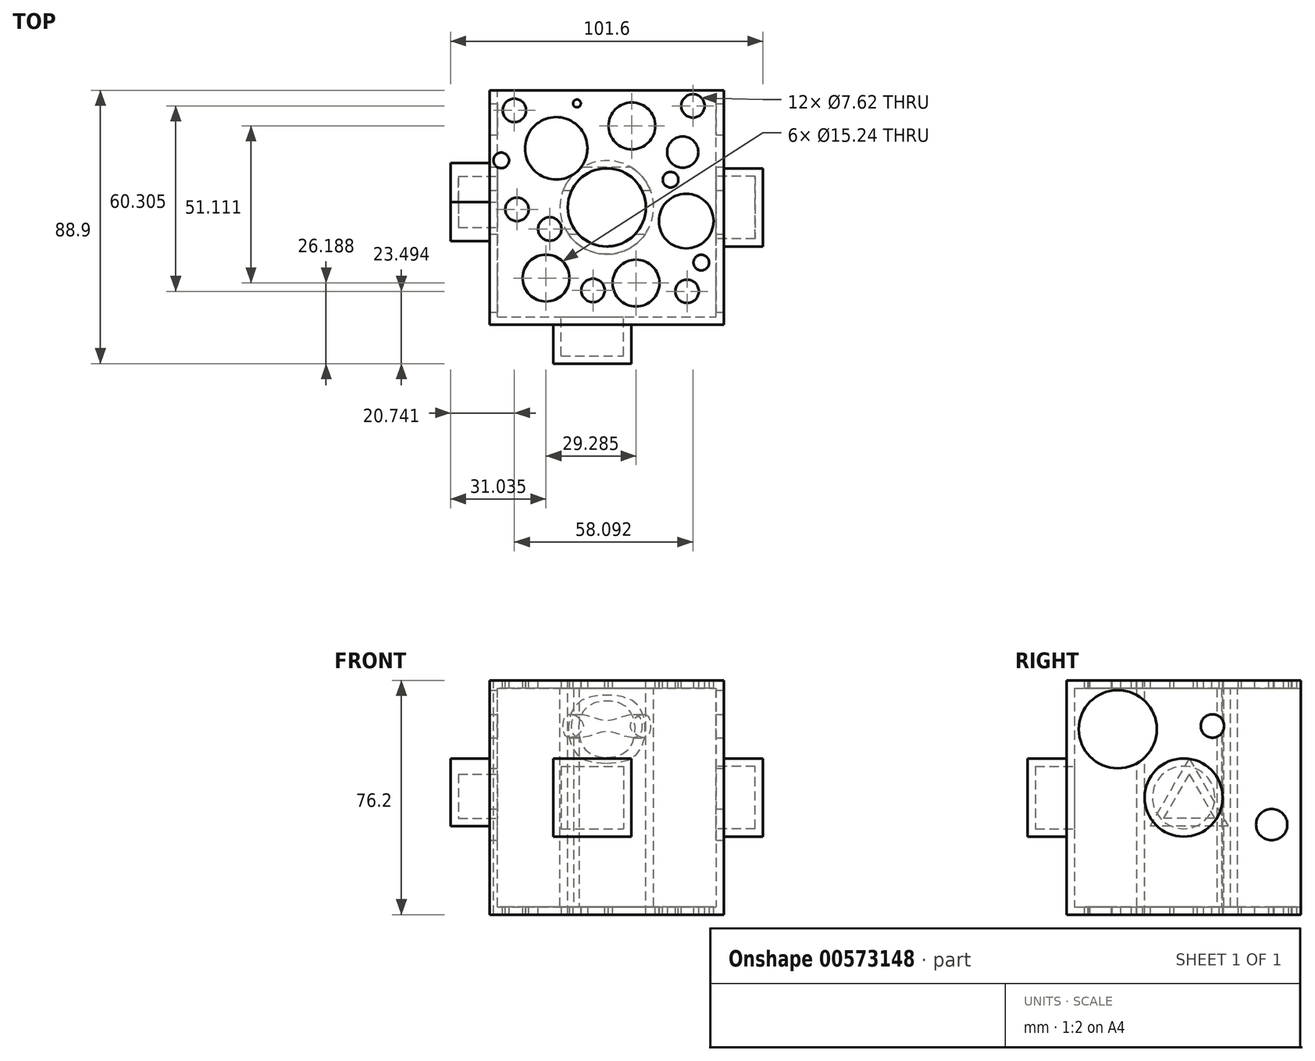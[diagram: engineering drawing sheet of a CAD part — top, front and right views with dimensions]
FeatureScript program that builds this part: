
annotation { "Feature Type Name" : "Feature", "Feature Type Description" : "" }
export const myFeature = defineFeature(function(context is Context, id is Id, definition is map)
    precondition{}
    {
        {
            var Q0;
            Q0=qCreatedBy(makeId("Front.planeOp"),FACE);
            var sketch = newSketch(context, id + "F0", { "sketchPlane" : qUnion([Q0])});
            skLineSegment(sketch, "E0.bottom", {"start": v(-76.2, 76.2) * mm, "end": v(0, 76.2) * mm});
            skLineSegment(sketch, "E0.top", {"start": v(-76.2, 0) * mm, "end": v(0, 0) * mm});
            skLineSegment(sketch, "E0.left", {"start": v(-76.2, 76.2) * mm, "end": v(-76.2, 0) * mm});
            skLineSegment(sketch, "E0.right", {"start": v(0, 76.2) * mm, "end": v(0, 0) * mm});
            skSolve(sketch);
        }
        {
            var Q0;
            Q0=makeQuery(id+"F0.imprint","IMPRINT",FACE,{"disambiguationData":[TD([[makeQuery(id+"F0.imprint","IMPRINT",EDGE,{"derivedFrom":sQuery(id+"F0.wireOp",EDGE,"E0.bottom")}),-1.0]])]});
            extrude(context, id + "F1", {"entities" : qUnion([Q0]), "depth" : 76.2 * mm, "offsetDistance" : 25.4 * mm});
        }
        {
            var Q0;
            Q0=makeQuery(id+"F1.opExtrude","CAP_FACE",FACE,{"disambiguationData":[OSD([sQuery(id+"F0.wireOp",EDGE,"E0.bottom"),sQuery(id+"F0.wireOp",EDGE,"E0.top"),sQuery(id+"F0.wireOp",EDGE,"E0.left"),sQuery(id+"F0.wireOp",EDGE,"E0.right")])],"isStart":false});
            var sketch = newSketch(context, id + "F2", { "sketchPlane" : qUnion([Q0])});
            skLineSegment(sketch, "E1.bottom", {"start": v(-55.52, 50.8) * mm, "end": v(-30.12, 50.8) * mm});
            skLineSegment(sketch, "E1.top", {"start": v(-55.52, 25.4) * mm, "end": v(-30.12, 25.4) * mm});
            skLineSegment(sketch, "E1.left", {"start": v(-55.52, 50.8) * mm, "end": v(-55.52, 25.4) * mm});
            skLineSegment(sketch, "E1.right", {"start": v(-30.12, 50.8) * mm, "end": v(-30.12, 25.4) * mm});
            skSolve(sketch);
        }
        {
            var Q0;
            Q0=makeQuery(id+"F2.imprint","IMPRINT",FACE,{"disambiguationData":[TD([[makeQuery(id+"F2.imprint","IMPRINT",EDGE,{"derivedFrom":sQuery(id+"F2.wireOp",EDGE,"E1.bottom")}),-1.0]])]});
            extrude(context, id + "F3", {"entities" : qUnion([Q0]), "operationType" : NewBodyOperationType.ADD, "depth" : 12.7 * mm, "offsetDistance" : 25.4 * mm});
        }
        {
            var Q0;
            Q0=makeQuery(id+"F1.opExtrude","SWEPT_FACE",FACE,{"disambiguationData":[OSD([sQuery(id+"F0.wireOp",EDGE,"E0.right")])]});
            var sketch = newSketch(context, id + "F4", { "sketchPlane" : qUnion([Q0])});
            skCircle(sketch, "E2", {"center": v(-38.1, 38.1) * mm, "radius": 12.7 * mm});
            skSolve(sketch);
        }
        {
            var Q0;
            Q0=makeQuery(id+"F4.imprint","IMPRINT",FACE,{"disambiguationData":[TD([[makeQuery(id+"F4.imprint","IMPRINT",EDGE,{"derivedFrom":sQuery(id+"F4.wireOp",EDGE,"E2")}),1.0]])]});
            extrude(context, id + "F5", {"entities" : qUnion([Q0]), "operationType" : NewBodyOperationType.ADD, "depth" : 12.7 * mm, "offsetDistance" : 25.4 * mm});
        }
        {
            var Q0;
            Q0=makeQuery(id+"F1.opExtrude","SWEPT_FACE",FACE,{"disambiguationData":[OSD([sQuery(id+"F0.wireOp",EDGE,"E0.bottom")])]});
            var sketch = newSketch(context, id + "F6", { "sketchPlane" : qUnion([Q0])});
            skPoint(sketch, "E3", {"position": v(-38.1, -38.1) * mm});
            skSolve(sketch);
        }
        {
            var Q0;
            Q0=sQuery(id+"F6.wireOp",VERTEX,"E3");
            var Q1;
            Q1=makeQuery(id+"F1.opExtrude","SWEPT_BODY",BODY,{"disambiguationData":[OSD([sQuery(id+"F0.wireOp",EDGE,"E0.bottom"),sQuery(id+"F0.wireOp",EDGE,"E0.top"),sQuery(id+"F0.wireOp",EDGE,"E0.left"),sQuery(id+"F0.wireOp",EDGE,"E0.right")])]});
            hole(context, id + "F7", {"style" : HoleStyle.SIMPLE, "endStyle" : HoleEndStyle.THROUGH, "holeDiameter" : 25.4 * mm, "isTappedThrough" : true, "tappedDepth" : 12.7 * mm, "tapClearance" : 3, "locations" : qUnion([Q0]), "scope" : qUnion([Q1])});
        }
        {
            var Q0;
            Q0=makeQuery(id+"F1.opExtrude","SWEPT_FACE",FACE,{"disambiguationData":[OSD([sQuery(id+"F0.wireOp",EDGE,"E0.left")])]});
            var sketch = newSketch(context, id + "F8", { "sketchPlane" : qUnion([Q0])});
            skLineSegment(sketch, "E4", {"start": v(36.34, 50.8) * mm, "end": v(23.64, 28.8) * mm});
            skLineSegment(sketch, "E5", {"start": v(23.64, 28.8) * mm, "end": v(49.04, 28.8) * mm});
            skLineSegment(sketch, "E6", {"start": v(36.34, 50.8) * mm, "end": v(49.04, 28.8) * mm});
            skSolve(sketch);
        }
        {
            var Q0;
            Q0=makeQuery(id+"F8.imprint","IMPRINT",FACE,{"disambiguationData":[TD([[makeQuery(id+"F8.imprint","IMPRINT",EDGE,{"derivedFrom":sQuery(id+"F8.wireOp",EDGE,"E4")}),1.0]])]});
            extrude(context, id + "F9", {"entities" : qUnion([Q0]), "operationType" : NewBodyOperationType.ADD, "depth" : 12.7 * mm, "offsetDistance" : 25.4 * mm});
        }
        {
            var Q0;
            Q0=makeQuery(id+"F1.opExtrude","CAP_FACE",FACE,{"disambiguationData":[OSD([sQuery(id+"F0.wireOp",EDGE,"E0.bottom"),sQuery(id+"F0.wireOp",EDGE,"E0.top"),sQuery(id+"F0.wireOp",EDGE,"E0.left"),sQuery(id+"F0.wireOp",EDGE,"E0.right")])],"isStart":true});
            var sketch = newSketch(context, id + "F10", { "sketchPlane" : qUnion([Q0])});
            skSolve(sketch);
        }
        {
            var Q0;
            Q0=makeQuery(id+"F1.opExtrude","CAP_FACE",FACE,{"disambiguationData":[OSD([sQuery(id+"F0.wireOp",EDGE,"E0.bottom"),sQuery(id+"F0.wireOp",EDGE,"E0.top"),sQuery(id+"F0.wireOp",EDGE,"E0.left"),sQuery(id+"F0.wireOp",EDGE,"E0.right")])],"isStart":true});
            shell(context, id + "F11", {"entities" : qUnion([Q0]), "thickness" : 2.54 * mm});
        }
        {
            var Q0;
            Q0=makeQuery(id+"F1.opExtrude","SWEPT_FACE",FACE,{"disambiguationData":[OSD([sQuery(id+"F0.wireOp",EDGE,"E0.top")])]});
            var sketch = newSketch(context, id + "F12", { "sketchPlane" : qUnion([Q0])});
            skPoint(sketch, "E7", {"position": v(-7.34, 56.06) * mm});
            skSolve(sketch);
        }
        {
            var Q0;
            Q0=sQuery(id+"F12.wireOp",VERTEX,"E7");
            var Q1;
            Q1=makeQuery(id+"F1.opExtrude","SWEPT_BODY",BODY,{"disambiguationData":[OSD([sQuery(id+"F0.wireOp",EDGE,"E0.bottom"),sQuery(id+"F0.wireOp",EDGE,"E0.top"),sQuery(id+"F0.wireOp",EDGE,"E0.left"),sQuery(id+"F0.wireOp",EDGE,"E0.right")])]});
            hole(context, id + "F13", {"style" : HoleStyle.SIMPLE, "endStyle" : HoleEndStyle.THROUGH, "holeDiameter" : 5.08 * mm, "majorDiameter" : 6.35 * mm, "isTappedThrough" : true, "tappedDepth" : 12.7 * mm, "tapClearance" : 3, "locations" : qUnion([Q0]), "scope" : qUnion([Q1])});
        }
        {
            var Q0;
            Q0=makeQuery(id+"F1.opExtrude","SWEPT_FACE",FACE,{"disambiguationData":[OSD([sQuery(id+"F0.wireOp",EDGE,"E0.top")])]});
            var sketch = newSketch(context, id + "F14", { "sketchPlane" : qUnion([Q0])});
            skPoint(sketch, "E8", {"position": v(-13.4, 20.13) * mm});
            skSolve(sketch);
        }
        {
            var Q0;
            Q0=sQuery(id+"F14.wireOp",VERTEX,"E8");
            var Q1;
            Q1=makeQuery(id+"F1.opExtrude","SWEPT_BODY",BODY,{"disambiguationData":[OSD([sQuery(id+"F0.wireOp",EDGE,"E0.bottom"),sQuery(id+"F0.wireOp",EDGE,"E0.top"),sQuery(id+"F0.wireOp",EDGE,"E0.left"),sQuery(id+"F0.wireOp",EDGE,"E0.right")])]});
            hole(context, id + "F15", {"style" : HoleStyle.SIMPLE, "endStyle" : HoleEndStyle.THROUGH, "holeDiameter" : 10.16 * mm, "majorDiameter" : 6.35 * mm, "isTappedThrough" : true, "tappedDepth" : 12.7 * mm, "tapClearance" : 3, "locations" : qUnion([Q0]), "scope" : qUnion([Q1])});
        }
        {
            var Q0;
            Q0=makeQuery(id+"F1.opExtrude","SWEPT_FACE",FACE,{"disambiguationData":[OSD([sQuery(id+"F0.wireOp",EDGE,"E0.top")])]});
            var sketch = newSketch(context, id + "F16", { "sketchPlane" : qUnion([Q0])});
            skPoint(sketch, "E9", {"position": v(-54.55, 18.9) * mm});
            skSolve(sketch);
        }
        {
            var Q0;
            Q0=sQuery(id+"F16.wireOp",VERTEX,"E9");
            var Q1;
            Q1=makeQuery(id+"F1.opExtrude","SWEPT_BODY",BODY,{"disambiguationData":[OSD([sQuery(id+"F0.wireOp",EDGE,"E0.bottom"),sQuery(id+"F0.wireOp",EDGE,"E0.top"),sQuery(id+"F0.wireOp",EDGE,"E0.left"),sQuery(id+"F0.wireOp",EDGE,"E0.right")])]});
            hole(context, id + "F17", {"style" : HoleStyle.SIMPLE, "endStyle" : HoleEndStyle.THROUGH, "holeDiameter" : 20.32 * mm, "majorDiameter" : 6.35 * mm, "isTappedThrough" : true, "tappedDepth" : 12.7 * mm, "tapClearance" : 3, "locations" : qUnion([Q0]), "scope" : qUnion([Q1])});
        }
        {
            var Q0;
            Q0=makeQuery(id+"F1.opExtrude","SWEPT_FACE",FACE,{"disambiguationData":[OSD([sQuery(id+"F0.wireOp",EDGE,"E0.top")])]});
            var sketch = newSketch(context, id + "F18", { "sketchPlane" : qUnion([Q0])});
            skPoint(sketch, "E10", {"position": v(-57.87, 61.09) * mm});
            skSolve(sketch);
        }
        {
            var Q0;
            Q0=sQuery(id+"F18.wireOp",VERTEX,"E10");
            var Q1;
            Q1=makeQuery(id+"F1.opExtrude","SWEPT_BODY",BODY,{"disambiguationData":[OSD([sQuery(id+"F0.wireOp",EDGE,"E0.bottom"),sQuery(id+"F0.wireOp",EDGE,"E0.top"),sQuery(id+"F0.wireOp",EDGE,"E0.left"),sQuery(id+"F0.wireOp",EDGE,"E0.right")])]});
            hole(context, id + "F19", {"style" : HoleStyle.SIMPLE, "endStyle" : HoleEndStyle.THROUGH, "holeDiameter" : 15.24 * mm, "majorDiameter" : 6.35 * mm, "isTappedThrough" : true, "tappedDepth" : 12.7 * mm, "tapClearance" : 3, "locations" : qUnion([Q0]), "scope" : qUnion([Q1])});
        }
        {
            var Q0;
            Q0=makeQuery(id+"F1.opExtrude","SWEPT_FACE",FACE,{"disambiguationData":[OSD([sQuery(id+"F0.wireOp",EDGE,"E0.bottom")])]});
            var sketch = newSketch(context, id + "F20", { "sketchPlane" : qUnion([Q0])});
            skPoint(sketch, "E11", {"position": v(-67.32, -38.75) * mm});
            skSolve(sketch);
        }
        {
            var Q0;
            Q0=sQuery(id+"F20.wireOp",VERTEX,"E11");
            var Q1;
            Q1=makeQuery(id+"F1.opExtrude","SWEPT_BODY",BODY,{"disambiguationData":[OSD([sQuery(id+"F0.wireOp",EDGE,"E0.bottom"),sQuery(id+"F0.wireOp",EDGE,"E0.top"),sQuery(id+"F0.wireOp",EDGE,"E0.left"),sQuery(id+"F0.wireOp",EDGE,"E0.right")])]});
            hole(context, id + "F21", {"style" : HoleStyle.SIMPLE, "endStyle" : HoleEndStyle.THROUGH, "holeDiameter" : 7.62 * mm, "majorDiameter" : 6.35 * mm, "isTappedThrough" : true, "tappedDepth" : 12.7 * mm, "tapClearance" : 3, "locations" : qUnion([Q0]), "scope" : qUnion([Q1])});
        }
        {
            var Q0;
            Q0=makeQuery(id+"F1.opExtrude","SWEPT_FACE",FACE,{"disambiguationData":[OSD([sQuery(id+"F0.wireOp",EDGE,"E0.bottom")])]});
            var sketch = newSketch(context, id + "F22", { "sketchPlane" : qUnion([Q0])});
            skPoint(sketch, "E12", {"position": v(-28.58, -62.71) * mm});
            skSolve(sketch);
        }
        {
            var Q0;
            Q0=sQuery(id+"F22.wireOp",VERTEX,"E12");
            var Q1;
            Q1=makeQuery(id+"F1.opExtrude","SWEPT_BODY",BODY,{"disambiguationData":[OSD([sQuery(id+"F0.wireOp",EDGE,"E0.bottom"),sQuery(id+"F0.wireOp",EDGE,"E0.top"),sQuery(id+"F0.wireOp",EDGE,"E0.left"),sQuery(id+"F0.wireOp",EDGE,"E0.right")])]});
            hole(context, id + "F23", {"style" : HoleStyle.SIMPLE, "endStyle" : HoleEndStyle.THROUGH, "holeDiameter" : 15.24 * mm, "majorDiameter" : 6.35 * mm, "isTappedThrough" : true, "tappedDepth" : 12.7 * mm, "tapClearance" : 3, "locations" : qUnion([Q0]), "scope" : qUnion([Q1])});
        }
        {
            var Q0;
            Q0=makeQuery(id+"F1.opExtrude","SWEPT_FACE",FACE,{"disambiguationData":[OSD([sQuery(id+"F0.wireOp",EDGE,"E0.bottom")])]});
            var sketch = newSketch(context, id + "F24", { "sketchPlane" : qUnion([Q0])});
            skPoint(sketch, "E13", {"position": v(-29.94, -11.6) * mm});
            skSolve(sketch);
        }
        {
            var Q0;
            Q0=sQuery(id+"F24.wireOp",VERTEX,"E13");
            var Q1;
            Q1=makeQuery(id+"F1.opExtrude","SWEPT_BODY",BODY,{"disambiguationData":[OSD([sQuery(id+"F0.wireOp",EDGE,"E0.bottom"),sQuery(id+"F0.wireOp",EDGE,"E0.top"),sQuery(id+"F0.wireOp",EDGE,"E0.left"),sQuery(id+"F0.wireOp",EDGE,"E0.right")])]});
            hole(context, id + "F25", {"style" : HoleStyle.SIMPLE, "endStyle" : HoleEndStyle.THROUGH, "holeDiameter" : 15.24 * mm, "majorDiameter" : 6.35 * mm, "isTappedThrough" : true, "tappedDepth" : 12.7 * mm, "tapClearance" : 3, "locations" : qUnion([Q0]), "scope" : qUnion([Q1])});
        }
        {
            var Q0;
            Q0=makeQuery(id+"F1.opExtrude","SWEPT_FACE",FACE,{"disambiguationData":[OSD([sQuery(id+"F0.wireOp",EDGE,"E0.bottom")])]});
            var sketch = newSketch(context, id + "F26", { "sketchPlane" : qUnion([Q0])});
            skPoint(sketch, "E14", {"position": v(-12.26, -42.55) * mm});
            skSolve(sketch);
        }
        {
            var Q0;
            Q0=sQuery(id+"F26.wireOp",VERTEX,"E14");
            var Q1;
            Q1=makeQuery(id+"F1.opExtrude","SWEPT_BODY",BODY,{"disambiguationData":[OSD([sQuery(id+"F0.wireOp",EDGE,"E0.bottom"),sQuery(id+"F0.wireOp",EDGE,"E0.top"),sQuery(id+"F0.wireOp",EDGE,"E0.left"),sQuery(id+"F0.wireOp",EDGE,"E0.right")])]});
            hole(context, id + "F27", {"style" : HoleStyle.SIMPLE, "endStyle" : HoleEndStyle.THROUGH, "holeDiameter" : 17.78 * mm, "majorDiameter" : 6.35 * mm, "isTappedThrough" : true, "tappedDepth" : 12.7 * mm, "tapClearance" : 3, "locations" : qUnion([Q0]), "scope" : qUnion([Q1])});
        }
        {
            var Q0;
            Q0=makeQuery(id+"F1.opExtrude","SWEPT_FACE",FACE,{"disambiguationData":[OSD([sQuery(id+"F0.wireOp",EDGE,"E0.bottom")])]});
            var sketch = newSketch(context, id + "F28", { "sketchPlane" : qUnion([Q0])});
            skPoint(sketch, "E15", {"position": v(-17.35, -29.13) * mm});
            skSolve(sketch);
        }
        {
            var Q0;
            Q0=sQuery(id+"F28.wireOp",VERTEX,"E15");
            var Q1;
            Q1=makeQuery(id+"F1.opExtrude","SWEPT_BODY",BODY,{"disambiguationData":[OSD([sQuery(id+"F0.wireOp",EDGE,"E0.bottom"),sQuery(id+"F0.wireOp",EDGE,"E0.top"),sQuery(id+"F0.wireOp",EDGE,"E0.left"),sQuery(id+"F0.wireOp",EDGE,"E0.right")])]});
            hole(context, id + "F29", {"style" : HoleStyle.SIMPLE, "endStyle" : HoleEndStyle.THROUGH, "holeDiameter" : 5.08 * mm, "majorDiameter" : 6.35 * mm, "isTappedThrough" : true, "tappedDepth" : 12.7 * mm, "tapClearance" : 3, "locations" : qUnion([Q0]), "scope" : qUnion([Q1])});
        }
        {
            var Q0;
            Q0=makeQuery(id+"F1.opExtrude","SWEPT_FACE",FACE,{"disambiguationData":[OSD([sQuery(id+"F0.wireOp",EDGE,"E0.bottom")])]});
            var sketch = newSketch(context, id + "F30", { "sketchPlane" : qUnion([Q0])});
            skPoint(sketch, "E16", {"position": v(-56.64, -45.12) * mm});
            skSolve(sketch);
        }
        {
            var Q0;
            Q0=sQuery(id+"F30.wireOp",VERTEX,"E16");
            var Q1;
            Q1=makeQuery(id+"F1.opExtrude","SWEPT_BODY",BODY,{"disambiguationData":[OSD([sQuery(id+"F0.wireOp",EDGE,"E0.bottom"),sQuery(id+"F0.wireOp",EDGE,"E0.top"),sQuery(id+"F0.wireOp",EDGE,"E0.left"),sQuery(id+"F0.wireOp",EDGE,"E0.right")])]});
            hole(context, id + "F31", {"style" : HoleStyle.SIMPLE, "endStyle" : HoleEndStyle.THROUGH, "holeDiameter" : 7.62 * mm, "majorDiameter" : 6.35 * mm, "isTappedThrough" : true, "tappedDepth" : 12.7 * mm, "tapClearance" : 3, "locations" : qUnion([Q0]), "scope" : qUnion([Q1])});
        }
        {
            var Q0;
            Q0=makeQuery(id+"F1.opExtrude","SWEPT_FACE",FACE,{"disambiguationData":[OSD([sQuery(id+"F0.wireOp",EDGE,"E0.bottom")])]});
            var sketch = newSketch(context, id + "F32", { "sketchPlane" : qUnion([Q0])});
            skPoint(sketch, "E17", {"position": v(-10.07, -5.1) * mm});
            skSolve(sketch);
        }
        {
            var Q0;
            Q0=sQuery(id+"F32.wireOp",VERTEX,"E17");
            var Q1;
            Q1=makeQuery(id+"F1.opExtrude","SWEPT_BODY",BODY,{"disambiguationData":[OSD([sQuery(id+"F0.wireOp",EDGE,"E0.bottom"),sQuery(id+"F0.wireOp",EDGE,"E0.top"),sQuery(id+"F0.wireOp",EDGE,"E0.left"),sQuery(id+"F0.wireOp",EDGE,"E0.right")])]});
            hole(context, id + "F33", {"style" : HoleStyle.SIMPLE, "endStyle" : HoleEndStyle.THROUGH, "holeDiameter" : 7.62 * mm, "majorDiameter" : 6.35 * mm, "isTappedThrough" : true, "tappedDepth" : 12.7 * mm, "tapClearance" : 3, "locations" : qUnion([Q0]), "scope" : qUnion([Q1])});
        }
        {
            var Q0;
            Q0=makeQuery(id+"F1.opExtrude","SWEPT_FACE",FACE,{"disambiguationData":[OSD([sQuery(id+"F0.wireOp",EDGE,"E0.bottom")])]});
            var sketch = newSketch(context, id + "F34", { "sketchPlane" : qUnion([Q0])});
            skPoint(sketch, "E18", {"position": v(-47.8, -4.3) * mm});
            skSolve(sketch);
        }
        {
            var Q0;
            Q0=sQuery(id+"F34.wireOp",VERTEX,"E18");
            var Q1;
            Q1=makeQuery(id+"F1.opExtrude","SWEPT_BODY",BODY,{"disambiguationData":[OSD([sQuery(id+"F0.wireOp",EDGE,"E0.bottom"),sQuery(id+"F0.wireOp",EDGE,"E0.top"),sQuery(id+"F0.wireOp",EDGE,"E0.left"),sQuery(id+"F0.wireOp",EDGE,"E0.right")])]});
            hole(context, id + "F35", {"style" : HoleStyle.SIMPLE, "endStyle" : HoleEndStyle.THROUGH, "holeDiameter" : 2.54 * mm, "majorDiameter" : 6.35 * mm, "isTappedThrough" : true, "tappedDepth" : 12.7 * mm, "tapClearance" : 3, "locations" : qUnion([Q0]), "scope" : qUnion([Q1])});
        }
        {
            var Q0;
            Q0=makeQuery(id+"F1.opExtrude","SWEPT_FACE",FACE,{"disambiguationData":[OSD([sQuery(id+"F0.wireOp",EDGE,"E0.bottom")])]});
            var sketch = newSketch(context, id + "F36", { "sketchPlane" : qUnion([Q0])});
            skPoint(sketch, "E19", {"position": v(-42.59, -65.11) * mm});
            skSolve(sketch);
        }
        {
            var Q0;
            Q0=sQuery(id+"F36.wireOp",VERTEX,"E19");
            var Q1;
            Q1=makeQuery(id+"F1.opExtrude","SWEPT_BODY",BODY,{"disambiguationData":[OSD([sQuery(id+"F0.wireOp",EDGE,"E0.bottom"),sQuery(id+"F0.wireOp",EDGE,"E0.top"),sQuery(id+"F0.wireOp",EDGE,"E0.left"),sQuery(id+"F0.wireOp",EDGE,"E0.right")])]});
            hole(context, id + "F37", {"style" : HoleStyle.SIMPLE, "endStyle" : HoleEndStyle.THROUGH, "holeDiameter" : 7.62 * mm, "majorDiameter" : 6.35 * mm, "isTappedThrough" : true, "tappedDepth" : 12.7 * mm, "tapClearance" : 3, "locations" : qUnion([Q0]), "scope" : qUnion([Q1])});
        }
        {
            var Q0;
            Q0=makeQuery(id+"F1.opExtrude","SWEPT_FACE",FACE,{"disambiguationData":[OSD([sQuery(id+"F0.wireOp",EDGE,"E0.bottom")])]});
            var sketch = newSketch(context, id + "F38", { "sketchPlane" : qUnion([Q0])});
            skPoint(sketch, "E20", {"position": v(-11.98, -65.4) * mm});
            skSolve(sketch);
        }
        {
            var Q0;
            Q0=sQuery(id+"F38.wireOp",VERTEX,"E20");
            var Q1;
            Q1=makeQuery(id+"F1.opExtrude","SWEPT_BODY",BODY,{"disambiguationData":[OSD([sQuery(id+"F0.wireOp",EDGE,"E0.bottom"),sQuery(id+"F0.wireOp",EDGE,"E0.top"),sQuery(id+"F0.wireOp",EDGE,"E0.left"),sQuery(id+"F0.wireOp",EDGE,"E0.right")])]});
            hole(context, id + "F39", {"style" : HoleStyle.SIMPLE, "endStyle" : HoleEndStyle.THROUGH, "holeDiameter" : 7.62 * mm, "majorDiameter" : 6.35 * mm, "isTappedThrough" : true, "tappedDepth" : 12.7 * mm, "tapClearance" : 3, "locations" : qUnion([Q0]), "scope" : qUnion([Q1])});
        }
        {
            var Q0;
            Q0=makeQuery(id+"F1.opExtrude","SWEPT_FACE",FACE,{"disambiguationData":[OSD([sQuery(id+"F0.wireOp",EDGE,"E0.bottom")])]});
            var sketch = newSketch(context, id + "F40", { "sketchPlane" : qUnion([Q0])});
            skPoint(sketch, "E21", {"position": v(-68.16, -6.57) * mm});
            skSolve(sketch);
        }
        {
            var Q0;
            Q0=sQuery(id+"F40.wireOp",VERTEX,"E21");
            var Q1;
            Q1=makeQuery(id+"F1.opExtrude","SWEPT_BODY",BODY,{"disambiguationData":[OSD([sQuery(id+"F0.wireOp",EDGE,"E0.bottom"),sQuery(id+"F0.wireOp",EDGE,"E0.top"),sQuery(id+"F0.wireOp",EDGE,"E0.left"),sQuery(id+"F0.wireOp",EDGE,"E0.right")])]});
            hole(context, id + "F41", {"style" : HoleStyle.SIMPLE, "endStyle" : HoleEndStyle.THROUGH, "holeDiameter" : 7.62 * mm, "majorDiameter" : 6.35 * mm, "isTappedThrough" : true, "tappedDepth" : 12.7 * mm, "tapClearance" : 3, "locations" : qUnion([Q0]), "scope" : qUnion([Q1])});
        }
        {
            var Q0;
            Q0=makeQuery(id+"F1.opExtrude","SWEPT_FACE",FACE,{"disambiguationData":[OSD([sQuery(id+"F0.wireOp",EDGE,"E0.bottom")])]});
            var sketch = newSketch(context, id + "F42", { "sketchPlane" : qUnion([Q0])});
            skPoint(sketch, "E22", {"position": v(-72.44, -22.83) * mm});
            skSolve(sketch);
        }
        {
            var Q0;
            Q0=sQuery(id+"F42.wireOp",VERTEX,"E22");
            var Q1;
            Q1=makeQuery(id+"F1.opExtrude","SWEPT_BODY",BODY,{"disambiguationData":[OSD([sQuery(id+"F0.wireOp",EDGE,"E0.bottom"),sQuery(id+"F0.wireOp",EDGE,"E0.top"),sQuery(id+"F0.wireOp",EDGE,"E0.left"),sQuery(id+"F0.wireOp",EDGE,"E0.right")])]});
            hole(context, id + "F43", {"style" : HoleStyle.SIMPLE, "endStyle" : HoleEndStyle.THROUGH, "holeDiameter" : 5.08 * mm, "majorDiameter" : 6.35 * mm, "isTappedThrough" : true, "tappedDepth" : 12.7 * mm, "tapClearance" : 3, "locations" : qUnion([Q0]), "scope" : qUnion([Q1])});
        }
        {
            var Q0;
            Q0=makeQuery(id+"F1.opExtrude","SWEPT_FACE",FACE,{"disambiguationData":[OSD([sQuery(id+"F0.wireOp",EDGE,"E0.right")])]});
            var sketch = newSketch(context, id + "F44", { "sketchPlane" : qUnion([Q0])});
            skPoint(sketch, "E23", {"position": v(-59.52, 60.31) * mm});
            skSolve(sketch);
        }
        {
            var Q0;
            Q0=sQuery(id+"F44.wireOp",VERTEX,"E23");
            var Q1;
            Q1=makeQuery(id+"F1.opExtrude","SWEPT_BODY",BODY,{"disambiguationData":[OSD([sQuery(id+"F0.wireOp",EDGE,"E0.bottom"),sQuery(id+"F0.wireOp",EDGE,"E0.top"),sQuery(id+"F0.wireOp",EDGE,"E0.left"),sQuery(id+"F0.wireOp",EDGE,"E0.right")])]});
            hole(context, id + "F45", {"style" : HoleStyle.SIMPLE, "endStyle" : HoleEndStyle.THROUGH, "holeDiameter" : 25.4 * mm, "majorDiameter" : 6.35 * mm, "isTappedThrough" : true, "tappedDepth" : 12.7 * mm, "tapClearance" : 3, "locations" : qUnion([Q0]), "scope" : qUnion([Q1])});
        }
        {
            var Q0;
            Q0=makeQuery(id+"F1.opExtrude","SWEPT_FACE",FACE,{"disambiguationData":[OSD([sQuery(id+"F0.wireOp",EDGE,"E0.right")])]});
            var sketch = newSketch(context, id + "F46", { "sketchPlane" : qUnion([Q0])});
            skPoint(sketch, "E24", {"position": v(-28.73, 61.34) * mm});
            skSolve(sketch);
        }
        {
            var Q0;
            Q0=sQuery(id+"F46.wireOp",VERTEX,"E24");
            var Q1;
            Q1=makeQuery(id+"F1.opExtrude","SWEPT_BODY",BODY,{"disambiguationData":[OSD([sQuery(id+"F0.wireOp",EDGE,"E0.bottom"),sQuery(id+"F0.wireOp",EDGE,"E0.top"),sQuery(id+"F0.wireOp",EDGE,"E0.left"),sQuery(id+"F0.wireOp",EDGE,"E0.right")])]});
            hole(context, id + "F47", {"style" : HoleStyle.SIMPLE, "endStyle" : HoleEndStyle.THROUGH, "holeDiameter" : 7.62 * mm, "majorDiameter" : 6.35 * mm, "isTappedThrough" : true, "tappedDepth" : 12.7 * mm, "tapClearance" : 3, "locations" : qUnion([Q0]), "scope" : qUnion([Q1])});
        }
        {
            var Q0;
            Q0=makeQuery(id+"F1.opExtrude","SWEPT_FACE",FACE,{"disambiguationData":[OSD([sQuery(id+"F0.wireOp",EDGE,"E0.right")])]});
            var sketch = newSketch(context, id + "F48", { "sketchPlane" : qUnion([Q0])});
            skPoint(sketch, "E25", {"position": v(-9.46, 29.26) * mm});
            skSolve(sketch);
        }
        {
            var Q0;
            Q0=sQuery(id+"F48.wireOp",VERTEX,"E25");
            var Q1;
            Q1=makeQuery(id+"F1.opExtrude","SWEPT_BODY",BODY,{"disambiguationData":[OSD([sQuery(id+"F0.wireOp",EDGE,"E0.bottom"),sQuery(id+"F0.wireOp",EDGE,"E0.top"),sQuery(id+"F0.wireOp",EDGE,"E0.left"),sQuery(id+"F0.wireOp",EDGE,"E0.right")])]});
            hole(context, id + "F49", {"style" : HoleStyle.SIMPLE, "endStyle" : HoleEndStyle.THROUGH, "holeDiameter" : 10.16 * mm, "majorDiameter" : 6.35 * mm, "isTappedThrough" : true, "tappedDepth" : 12.7 * mm, "tapClearance" : 3, "locations" : qUnion([Q0]), "scope" : qUnion([Q1])});
        }
    });
